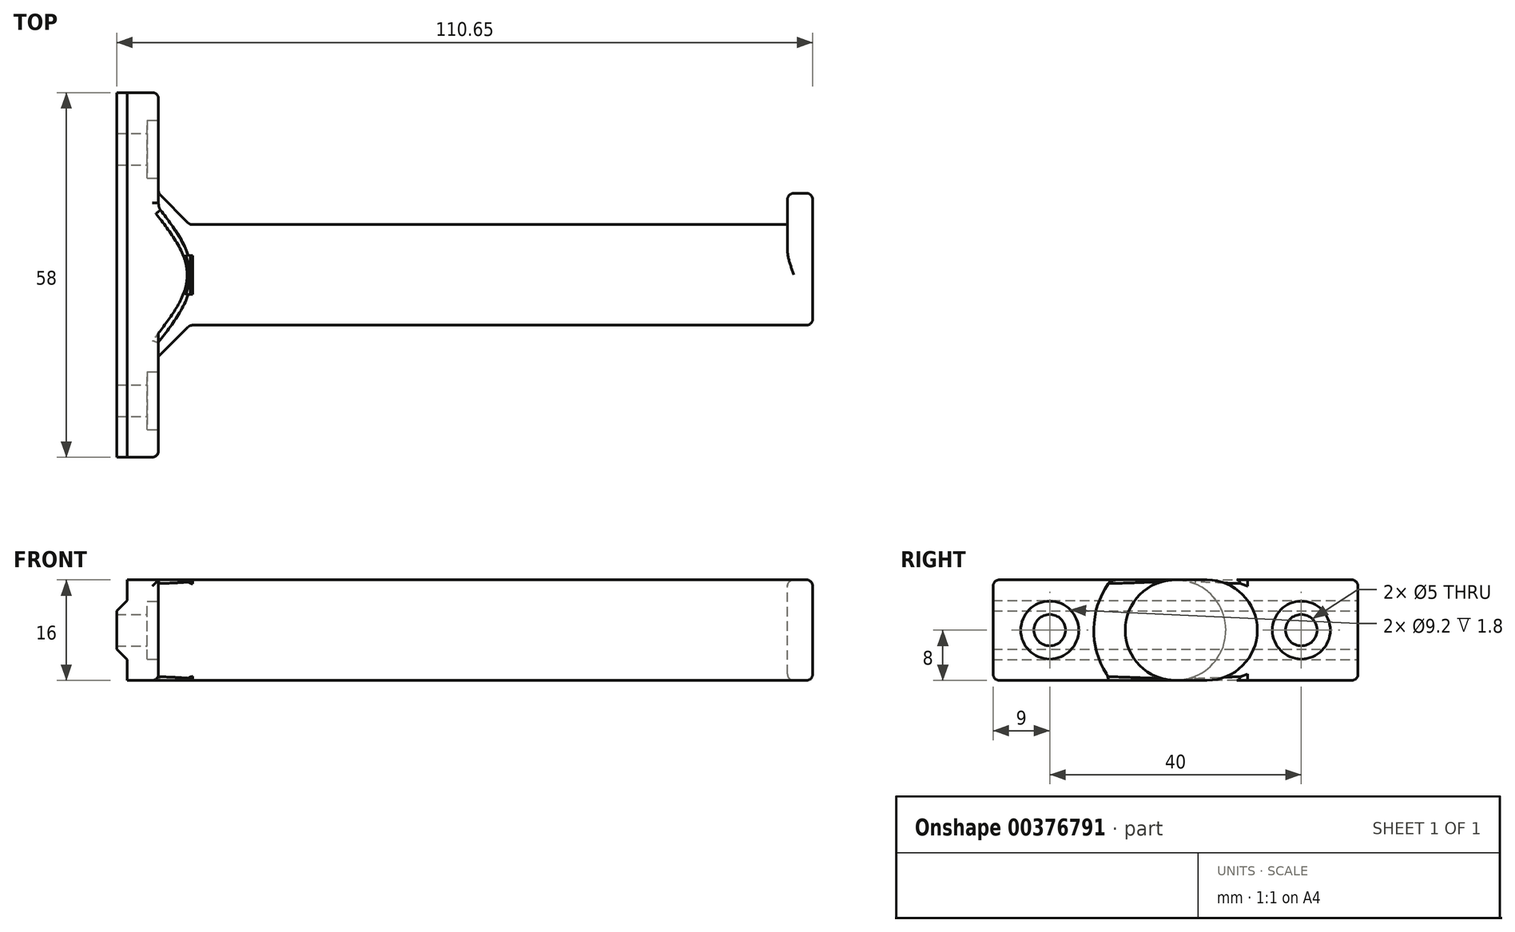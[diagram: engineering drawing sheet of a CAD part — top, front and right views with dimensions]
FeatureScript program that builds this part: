
annotation { "Feature Type Name" : "Feature", "Feature Type Description" : "" }
export const myFeature = defineFeature(function(context is Context, id is Id, definition is map)
    precondition{}
    {
        {
            var Q0;
            Q0=qCreatedBy(makeId("Right.planeOp"),FACE);
            var sketch = newSketch(context, id + "F0", { "sketchPlane" : qUnion([Q0])});
            skCircle(sketch, "E0", {"center": v(0, 0) * mm, "radius": 8 * mm});
            skSolve(sketch);
        }
        {
            var Q0;
            Q0 = qSketchRegion(id + "F0", true);
            extrude(context, id + "F1", {"entities" : qUnion([Q0]), "depth" : 95 * mm});
        }
        {
            var Q0;
            Q0=makeQuery(id+"F1.opExtrude","CAP_FACE",FACE,{"disambiguationData":[OSD([sQuery(id+"F0.wireOp",EDGE,"E0")])],"isStart":false});
            var sketch = newSketch(context, id + "F2", { "sketchPlane" : qUnion([Q0])});
            skArc(sketch, "E1", {"start": v(2.5, 7.6) * mm, "mid": v(-8, 0) * mm, "end": v(2.5, -7.6) * mm});
            skLineSegment(sketch, "E2", {"start": v(0, 0) * mm, "end": v(30.67, 0) * mm, "construction": true});
            skArc(sketch, "E3", {"start": v(5, -8) * mm, "mid": v(13, 0) * mm, "end": v(5, 8) * mm});
            skLineSegment(sketch, "E4", {"start": v(5, 8) * mm, "end": v(0, 8) * mm});
            skLineSegment(sketch, "E5", {"start": v(5, -8) * mm, "end": v(0, -8) * mm});
            skSolve(sketch);
        }
        {
            var Q0;
            Q0 = qSketchRegion(id + "F2", true);
            extrude(context, id + "F3", {"entities" : qUnion([Q0]), "operationType" : NewBodyOperationType.ADD, "depth" : 4 * mm});
        }
        {
            var Q0;
            Q0=qCreatedBy(makeId("Top.planeOp"),FACE);
            var sketch = newSketch(context, id + "F4", { "sketchPlane" : qUnion([Q0])});
            skLineSegment(sketch, "E6", {"start": v(0, 0) * mm, "end": v(0, 8) * mm});
            skLineSegment(sketch, "E7", {"start": v(0, 8) * mm, "end": v(-5, 13) * mm});
            skLineSegment(sketch, "E8", {"start": v(-5, 13) * mm, "end": v(-5, 0) * mm});
            skLineSegment(sketch, "E9", {"start": v(26.22, 0) * mm, "end": v(-29.93, 0) * mm, "construction": true});
            skLineSegment(sketch, "E10", {"start": v(0, 0) * mm, "end": v(-5, 0) * mm});
            skSolve(sketch);
        }
        {
            var Q0;
            Q0 = qSketchRegion(id + "F4", true);
            var Q1;
            Q1=sQuery(id+"F4.wireOp",EDGE,"E9");
            revolve(context, id + "F5", {"operationType" : NewBodyOperationType.ADD, "entities" : qUnion([Q0]), "axis" : qUnion([Q1]), "revolveType" : RevolveType.FULL});
        }
        {
            var Q0;
            Q0=makeQuery(id+"F5.opRevolve","SWEPT_FACE",FACE,{"disambiguationData":[OSD([sQuery(id+"F4.wireOp",EDGE,"E8")])]});
            var sketch = newSketch(context, id + "F6", { "sketchPlane" : qUnion([Q0])});
            skLineSegment(sketch, "E11", {"start": v(0, 0) * mm, "end": v(-25.76, 0) * mm, "construction": true});
            skLineSegment(sketch, "E12.bottom", {"start": v(-29, -8) * mm, "end": v(29, -8) * mm});
            skLineSegment(sketch, "E12.top", {"start": v(-29, 8) * mm, "end": v(29, 8) * mm});
            skLineSegment(sketch, "E12.left", {"start": v(-29, -8) * mm, "end": v(-29, 8) * mm});
            skLineSegment(sketch, "E12.right", {"start": v(29, -8) * mm, "end": v(29, 8) * mm});
            skPoint(sketch, "E12.middle", {"position": v(0, 0) * mm});
            skPoint(sketch, "E13", {"position": v(-20, 0) * mm});
            skPoint(sketch, "E14.MirrorP", {"position": v(20, 0) * mm});
            skSolve(sketch);
        }
        {
            var Q0;
            Q0 = qSketchRegion(id + "F6", true);
            extrude(context, id + "F7", {"entities" : qUnion([Q0]), "operationType" : NewBodyOperationType.ADD, "depth" : 5 * mm});
        }
        {
            var Q0;
            {var subQ0=sQuery(id+"F6.wireOp",EDGE,"E12.bottom");var subQ1=makeQuery(id+"F5.opRevolve","SWEPT_EDGE",EDGE,{"disambiguationData":[OSD([sQuery(id+"F4.wireOp",EDGE,"E7"),sQuery(id+"F4.wireOp",EDGE,"E8")])]});var subQ2=makeQuery(id+"F6.imprint","INTERSECT",VERTEX,{"disambiguationData":[OD(0.0)],"derivedFrom":[subQ1,subQ0]});Q0=makeQuery(id+"F6.imprint","IMPRINT",FACE,{"disambiguationData":[TD([[makeQuery(id+"F6.imprint","IMPRINT",EDGE,{"disambiguationData":[TD([[subQ2,-1.0]])],"derivedFrom":subQ0}),-1.0]])]});}
            var sketch = newSketch(context, id + "F8", { "sketchPlane" : qUnion([Q0])});
            skLineSegment(sketch, "E15.bottom", {"start": v(-35.92, -15.92) * mm, "end": v(35.92, -15.92) * mm});
            skLineSegment(sketch, "E15.top", {"start": v(-35.92, 15.92) * mm, "end": v(35.92, 15.92) * mm});
            skLineSegment(sketch, "E15.left", {"start": v(-35.92, -15.92) * mm, "end": v(-35.92, 15.92) * mm});
            skLineSegment(sketch, "E15.right", {"start": v(35.92, -15.92) * mm, "end": v(35.92, 15.92) * mm});
            skPoint(sketch, "E15.middle", {"position": v(0, 0) * mm});
            skLineSegment(sketch, "E16.bottom", {"start": v(-29, -8) * mm, "end": v(29, -8) * mm});
            skLineSegment(sketch, "E16.top", {"start": v(-29, 8) * mm, "end": v(29, 8) * mm});
            skLineSegment(sketch, "E16.left", {"start": v(-29, -8) * mm, "end": v(-29, 8) * mm});
            skLineSegment(sketch, "E16.right", {"start": v(29, -8) * mm, "end": v(29, 8) * mm});
            skSolve(sketch);
        }
        {
            var Q0;
            Q0 = qSketchRegion(id + "F8", true);
            extrude(context, id + "F9", {"entities" : qUnion([Q0]), "operationType" : NewBodyOperationType.REMOVE, "endBound" : BoundingType.THROUGH_ALL, "oppositeDirection" : true, "depth" : 25 * mm});
        }
        {
            var Q0;
            Q0=makeQuery(id+"F9.boolean.opBoolean","SPLIT",EDGE,{"disambiguationData":[OD(0.0)],"derivedFrom":makeQuery(id+"F5.boolean.opBoolean","MERGE",EDGE,{"derivedFrom":[makeQuery(id+"F1.opExtrude","CAP_EDGE",EDGE,{"disambiguationData":[OSD([sQuery(id+"F0.wireOp",EDGE,"E0")])],"isStart":true}),makeQuery(id+"F5.opRevolve","SWEPT_EDGE",EDGE,{"disambiguationData":[OSD([sQuery(id+"F4.wireOp",EDGE,"E6"),sQuery(id+"F4.wireOp",EDGE,"E7")])]})]})});
            var Q1;
            Q1=makeQuery(id+"F9.boolean.opBoolean","SPLIT",EDGE,{"disambiguationData":[OD(1.0)],"derivedFrom":makeQuery(id+"F5.boolean.opBoolean","MERGE",EDGE,{"derivedFrom":[makeQuery(id+"F1.opExtrude","CAP_EDGE",EDGE,{"disambiguationData":[OSD([sQuery(id+"F0.wireOp",EDGE,"E0")])],"isStart":true}),makeQuery(id+"F5.opRevolve","SWEPT_EDGE",EDGE,{"disambiguationData":[OSD([sQuery(id+"F4.wireOp",EDGE,"E6"),sQuery(id+"F4.wireOp",EDGE,"E7")])]})]})});
            var Q2;
            {var subQ0=sQuery(id+"F4.wireOp",EDGE,"E7");Q2=makeQuery(id+"F7.boolean.opBoolean","SPLIT",EDGE,{"disambiguationData":[topologyDisambiguationEdgeConnected([makeQuery(id+"F5.opRevolve","SWEPT_FACE",FACE,{"disambiguationData":[OSD([subQ0])]}),makeQuery(id+"F7.opExtrude","CAP_FACE",FACE,{"disambiguationData":[OSD([sQuery(id+"F6.wireOp",EDGE,"E12.bottom"),sQuery(id+"F6.wireOp",EDGE,"E12.top"),sQuery(id+"F6.wireOp",EDGE,"E12.left"),sQuery(id+"F6.wireOp",EDGE,"E12.right")])],"isStart":true})]),OD(0.0)],"derivedFrom":makeQuery(id+"F5.opRevolve","SWEPT_EDGE",EDGE,{"disambiguationData":[OSD([subQ0,sQuery(id+"F4.wireOp",EDGE,"E8")])]})});}
            var Q3;
            {var subQ0=sQuery(id+"F4.wireOp",EDGE,"E7");Q3=makeQuery(id+"F7.boolean.opBoolean","SPLIT",EDGE,{"disambiguationData":[topologyDisambiguationEdgeConnected([makeQuery(id+"F5.opRevolve","SWEPT_FACE",FACE,{"disambiguationData":[OSD([subQ0])]}),makeQuery(id+"F7.opExtrude","CAP_FACE",FACE,{"disambiguationData":[OSD([sQuery(id+"F6.wireOp",EDGE,"E12.bottom"),sQuery(id+"F6.wireOp",EDGE,"E12.top"),sQuery(id+"F6.wireOp",EDGE,"E12.left"),sQuery(id+"F6.wireOp",EDGE,"E12.right")])],"isStart":true})]),OD(1.0)],"derivedFrom":makeQuery(id+"F5.opRevolve","SWEPT_EDGE",EDGE,{"disambiguationData":[OSD([subQ0,sQuery(id+"F4.wireOp",EDGE,"E8")])]})});}
            var Q4;
            {var subQ0=sQuery(id+"F6.wireOp",EDGE,"E12.left");var subQ1=sQuery(id+"F6.wireOp",EDGE,"E12.top");var subQ2=makeQuery(id+"F7.opExtrude","CAP_FACE",FACE,{"disambiguationData":[OSD([sQuery(id+"F6.wireOp",EDGE,"E12.bottom"),subQ1,subQ0,sQuery(id+"F6.wireOp",EDGE,"E12.right")])],"isStart":true});var subQ3=makeQuery(id+"F7.opExtrude","SWEPT_FACE",FACE,{"disambiguationData":[OSD([subQ1])]});Q4=makeQuery(id+"F7.boolean.opBoolean","SPLIT",EDGE,{"disambiguationData":[topologyDisambiguationEdgeConnected([subQ2,subQ3]),TD([makeQuery(id+"F7.opExtrude","SWEPT_FACE",FACE,{"disambiguationData":[OSD([subQ0])]})])],"derivedFrom":makeQuery(id+"F7.opExtrude","CAP_EDGE",EDGE,{"disambiguationData":[OSD([subQ1])],"isStart":true})});}
            var Q5;
            Q5=makeQuery(id+"F7.opExtrude","CAP_EDGE",EDGE,{"disambiguationData":[OSD([sQuery(id+"F6.wireOp",EDGE,"E12.left")])],"isStart":true});
            var Q6;
            {var subQ0=sQuery(id+"F6.wireOp",EDGE,"E12.left");var subQ1=sQuery(id+"F6.wireOp",EDGE,"E12.bottom");var subQ2=makeQuery(id+"F7.opExtrude","CAP_FACE",FACE,{"disambiguationData":[OSD([subQ1,sQuery(id+"F6.wireOp",EDGE,"E12.top"),subQ0,sQuery(id+"F6.wireOp",EDGE,"E12.right")])],"isStart":true});var subQ3=makeQuery(id+"F7.opExtrude","SWEPT_FACE",FACE,{"disambiguationData":[OSD([subQ1])]});Q6=makeQuery(id+"F7.boolean.opBoolean","SPLIT",EDGE,{"disambiguationData":[topologyDisambiguationEdgeConnected([subQ3,subQ2]),TD([makeQuery(id+"F7.opExtrude","SWEPT_FACE",FACE,{"disambiguationData":[OSD([subQ0])]})])],"derivedFrom":makeQuery(id+"F7.opExtrude","CAP_EDGE",EDGE,{"disambiguationData":[OSD([subQ1])],"isStart":true})});}
            var Q7;
            Q7=makeQuery(id+"F9.boolean.opBoolean","INTERSECT",EDGE,{"disambiguationData":[OD(0.0)],"derivedFrom":[makeQuery(id+"F5.opRevolve","SWEPT_FACE",FACE,{"disambiguationData":[OSD([sQuery(id+"F4.wireOp",EDGE,"E7")])]}),makeQuery(id+"F9.opExtrude","SWEPT_FACE",FACE,{"disambiguationData":[OSD([sQuery(id+"F8.wireOp",EDGE,"E16.bottom")])]})]});
            var Q8;
            Q8=makeQuery(id+"F9.boolean.opBoolean","INTERSECT",EDGE,{"disambiguationData":[OD(1.0)],"derivedFrom":[makeQuery(id+"F5.opRevolve","SWEPT_FACE",FACE,{"disambiguationData":[OSD([sQuery(id+"F4.wireOp",EDGE,"E7")])]}),makeQuery(id+"F9.opExtrude","SWEPT_FACE",FACE,{"disambiguationData":[OSD([sQuery(id+"F8.wireOp",EDGE,"E16.bottom")])]})]});
            var Q9;
            Q9=makeQuery(id+"F9.boolean.opBoolean","INTERSECT",EDGE,{"disambiguationData":[OD(1.0)],"derivedFrom":[makeQuery(id+"F5.opRevolve","SWEPT_FACE",FACE,{"disambiguationData":[OSD([sQuery(id+"F4.wireOp",EDGE,"E7")])]}),makeQuery(id+"F9.opExtrude","SWEPT_FACE",FACE,{"disambiguationData":[OSD([sQuery(id+"F8.wireOp",EDGE,"E16.top")])]})]});
            var Q10;
            Q10=makeQuery(id+"F7.opExtrude","CAP_EDGE",EDGE,{"disambiguationData":[OSD([sQuery(id+"F6.wireOp",EDGE,"E12.right")])],"isStart":true});
            var Q11;
            Q11=makeQuery(id+"F7.opExtrude","SWEPT_EDGE",EDGE,{"disambiguationData":[OSD([sQuery(id+"F6.wireOp",EDGE,"E12.top"),sQuery(id+"F6.wireOp",EDGE,"E12.left")])]});
            var Q12;
            Q12=makeQuery(id+"F7.opExtrude","SWEPT_EDGE",EDGE,{"disambiguationData":[OSD([sQuery(id+"F6.wireOp",EDGE,"E12.bottom"),sQuery(id+"F6.wireOp",EDGE,"E12.left")])]});
            var Q13;
            Q13=makeQuery(id+"F7.opExtrude","SWEPT_EDGE",EDGE,{"disambiguationData":[OSD([sQuery(id+"F6.wireOp",EDGE,"E12.top"),sQuery(id+"F6.wireOp",EDGE,"E12.right")])]});
            var Q14;
            Q14=makeQuery(id+"F7.opExtrude","SWEPT_EDGE",EDGE,{"disambiguationData":[OSD([sQuery(id+"F6.wireOp",EDGE,"E12.bottom"),sQuery(id+"F6.wireOp",EDGE,"E12.right")])]});
            fillet(context, id + "F10", {"entities" : qUnion([Q0, Q1, Q2, Q3, Q4, Q5, Q6, Q7, Q8, Q9, Q10, Q11, Q12, Q13, Q14]), "radius" : 1 * mm, "tangentPropagation" : true, "allowEdgeOverflow" : false});
        }
        {
            var Q0;
            Q0=makeQuery(id+"F3.opExtrude","CAP_EDGE",EDGE,{"disambiguationData":[OSD([sQuery(id+"F2.wireOp",EDGE,"E3")])],"isStart":true});
            var Q1;
            Q1=makeQuery(id+"F3.opExtrude","CAP_EDGE",EDGE,{"disambiguationData":[OSD([sQuery(id+"F2.wireOp",EDGE,"E3")])],"isStart":false});
            var Q2;
            Q2=makeQuery(id+"F1.opExtrude","CAP_EDGE",EDGE,{"disambiguationData":[OSD([sQuery(id+"F0.wireOp",EDGE,"E0")])],"isStart":false});
            fillet(context, id + "F11", {"entities" : qUnion([Q0, Q1, Q2]), "radius" : 1 * mm, "tangentPropagation" : true, "allowEdgeOverflow" : false});
        }
        {
            var Q0;
            Q0=qCreatedBy(makeId("Front.planeOp"),FACE);
            var sketch = newSketch(context, id + "F12", { "sketchPlane" : qUnion([Q0])});
            skLineSegment(sketch, "E17", {"start": v(-11.65, 3.05) * mm, "end": v(-11.65, -3.05) * mm});
            skLineSegment(sketch, "E18", {"start": v(-11.65, -3.05) * mm, "end": v(-10, -4.7) * mm});
            skLineSegment(sketch, "E19", {"start": v(-10, -4.7) * mm, "end": v(-10, 4.7) * mm});
            skLineSegment(sketch, "E20", {"start": v(-10, 4.7) * mm, "end": v(-11.65, 3.05) * mm});
            skSolve(sketch);
        }
        {
            var Q0;
            Q0 = qSketchRegion(id + "F12", true);
            var Q1;
            Q1=makeQuery(id+"F7.opExtrude","SWEPT_FACE",FACE,{"disambiguationData":[OSD([sQuery(id+"F6.wireOp",EDGE,"E12.right")])]});
            var Q2;
            Q2=makeQuery(id+"F7.opExtrude","SWEPT_FACE",FACE,{"disambiguationData":[OSD([sQuery(id+"F6.wireOp",EDGE,"E12.left")])]});
            extrude(context, id + "F13", {"entities" : qUnion([Q0]), "operationType" : NewBodyOperationType.ADD, "endBound" : BoundingType.UP_TO_SURFACE, "endBoundEntityFace" : qUnion([Q1]), "depth" : 25 * mm, "hasSecondDirection" : true, "secondDirectionBound" : SecondDirectionBoundingType.UP_TO_SURFACE, "secondDirectionOppositeDirection" : true, "secondDirectionBoundEntityFace" : qUnion([Q2]), "secondDirectionDepth" : 25 * mm});
        }
        {
            var Q0;
            Q0=sQuery(id+"F6.wireOp",VERTEX,"E13");
            var Q1;
            Q1=sQuery(id+"F6.wireOp",VERTEX,"E14.MirrorP");
            var Q2;
            Q2=makeQuery(id+"F1.opExtrude","SWEPT_BODY",BODY,{"disambiguationData":[OSD([sQuery(id+"F0.wireOp",EDGE,"E0")])]});
            hole(context, id + "F14", {"style" : HoleStyle.C_BORE, "endStyle" : HoleEndStyle.BLIND, "oppositeDirection" : true, "holeDiameter" : 5 * mm, "cBoreDiameter" : 9.2 * mm, "cBoreDepth" : 1.8 * mm, "holeDepth" : 12 * mm, "isTappedThrough" : true, "tappedDepth" : 12 * mm, "tapClearance" : 3, "locations" : qUnion([Q0, Q1]), "scope" : qUnion([Q2])});
        }
    });
